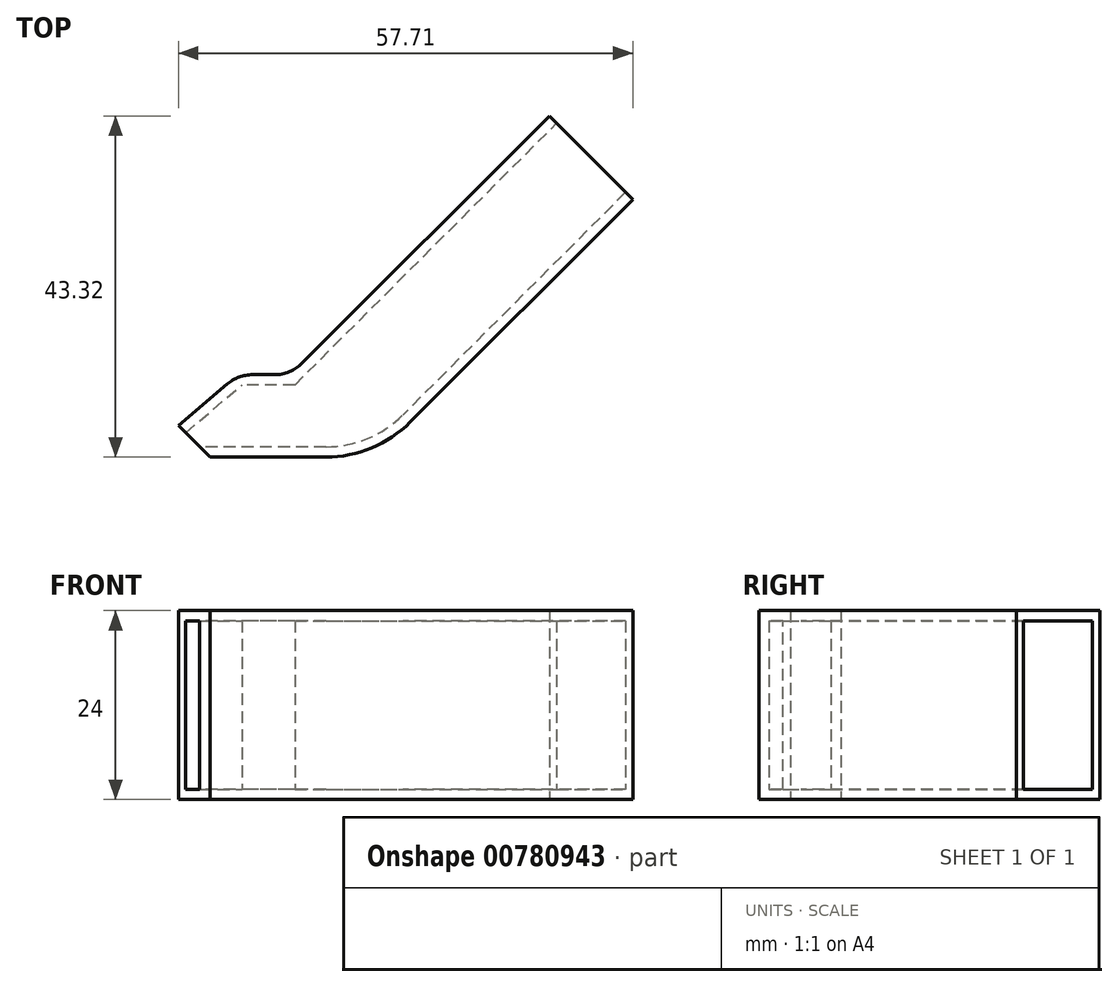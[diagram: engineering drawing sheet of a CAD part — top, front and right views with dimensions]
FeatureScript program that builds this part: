
annotation { "Feature Type Name" : "Feature", "Feature Type Description" : "" }
export const myFeature = defineFeature(function(context is Context, id is Id, definition is map)
    precondition{}
    {
        {
            var Q0;
            Q0=qCreatedBy(makeId("Top.planeOp"),FACE);
            var sketch = newSketch(context, id + "F0", { "sketchPlane" : qUnion([Q0])});
            skLineSegment(sketch, "E0", {"start": v(-34.12, -31.88) * mm, "end": v(-26.53, -25.42) * mm});
            skLineSegment(sketch, "E1", {"start": v(-19.88, -25.42) * mm, "end": v(12.99, 7.44) * mm});
            skLineSegment(sketch, "E2", {"start": v(12.99, 7.44) * mm, "end": v(23.6, -3.17) * mm});
            skLineSegment(sketch, "E3", {"start": v(23.6, -3.17) * mm, "end": v(-9.12, -35.88) * mm});
            skLineSegment(sketch, "E4", {"start": v(-9.12, -35.88) * mm, "end": v(-34.12, -35.88) * mm});
            skLineSegment(sketch, "E5", {"start": v(-34.12, -35.88) * mm, "end": v(-34.12, -31.88) * mm});
            skLineSegment(sketch, "E6", {"start": v(-19.88, -25.42) * mm, "end": v(-26.53, -25.42) * mm});
            skSolve(sketch);
        }
        {
            var Q0;
            Q0=makeQuery(id+"F0.imprint","IMPRINT",FACE,{"disambiguationData":[TD([[makeQuery(id+"F0.imprint","IMPRINT",EDGE,{"derivedFrom":sQuery(id+"F0.wireOp",EDGE,"E0")}),-1.0]])]});
            extrude(context, id + "F1", {"entities" : qUnion([Q0]), "depth" : 24 * mm, "offsetDistance" : 25 * mm});
        }
        {
            var Q0;
            Q0=makeQuery(id+"F1.opExtrude","SWEPT_EDGE",EDGE,{"disambiguationData":[OSD([sQuery(id+"F0.wireOp",EDGE,"E3"),sQuery(id+"F0.wireOp",EDGE,"E4")])]});
            fillet(context, id + "F2", {"entities" : qUnion([Q0]), "radius" : 15.1 * mm, "tangentPropagation" : true, "allowEdgeOverflow" : false});
        }
        {
            var Q0;
            Q0=makeQuery(id+"F1.opExtrude","SWEPT_FACE",FACE,{"disambiguationData":[OSD([sQuery(id+"F0.wireOp",EDGE,"E5")])]});
            var Q1;
            Q1=makeQuery(id+"F1.opExtrude","SWEPT_FACE",FACE,{"disambiguationData":[OSD([sQuery(id+"F0.wireOp",EDGE,"E2")])]});
            shell(context, id + "F3", {"entities" : qUnion([Q0, Q1]), "thickness" : 1.3 * mm});
        }
        {
            var Q0;
            Q0=makeQuery(id+"F1.opExtrude","CAP_FACE",FACE,{"disambiguationData":[OSD([sQuery(id+"F0.wireOp",EDGE,"E0"),sQuery(id+"F0.wireOp",EDGE,"E1"),sQuery(id+"F0.wireOp",EDGE,"E2"),sQuery(id+"F0.wireOp",EDGE,"E3"),sQuery(id+"F0.wireOp",EDGE,"E4"),sQuery(id+"F0.wireOp",EDGE,"E5")])],"isStart":false});
            var sketch = newSketch(context, id + "F4", { "sketchPlane" : qUnion([Q0])});
            skLineSegment(sketch, "E7", {"start": v(-34.12, -31.88) * mm, "end": v(-30.12, -35.88) * mm});
            skLineSegment(sketch, "E8", {"start": v(-30.12, -35.88) * mm, "end": v(-34.12, -35.88) * mm});
            skLineSegment(sketch, "E9", {"start": v(-34.12, -35.88) * mm, "end": v(-34.12, -31.88) * mm});
            skSolve(sketch);
        }
        {
            var Q0;
            Q0 = qSketchRegion(id + "F4", true);
            extrude(context, id + "F5", {"entities" : qUnion([Q0]), "operationType" : NewBodyOperationType.REMOVE, "endBound" : BoundingType.THROUGH_ALL, "oppositeDirection" : true, "depth" : 25 * mm, "offsetDistance" : 25 * mm});
        }
        {
            var Q0;
            Q0=makeQuery(id+"F1.opExtrude","SWEPT_EDGE",EDGE,{"disambiguationData":[OSD([sQuery(id+"F0.wireOp",EDGE,"E0"),sQuery(id+"F0.wireOp",EDGE,"E6")])]});
            var Q1;
            Q1=makeQuery(id+"F1.opExtrude","SWEPT_EDGE",EDGE,{"disambiguationData":[OSD([sQuery(id+"F0.wireOp",EDGE,"E1"),sQuery(id+"F0.wireOp",EDGE,"E6")])]});
            fillet(context, id + "F6", {"entities" : qUnion([Q0, Q1]), "radius" : 5 * mm, "tangentPropagation" : true, "allowEdgeOverflow" : false});
        }
    });
